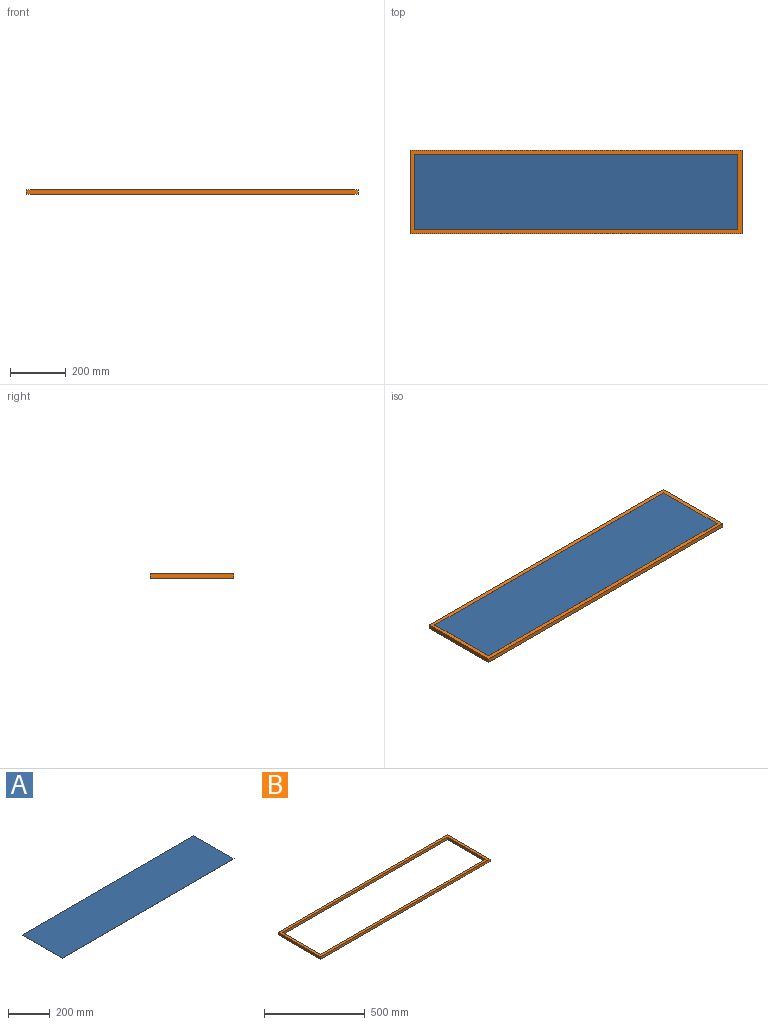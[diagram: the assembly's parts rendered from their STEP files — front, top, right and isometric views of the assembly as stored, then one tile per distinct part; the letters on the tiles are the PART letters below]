
ASSEMBLY  parts=2 mates=1
PART A: 6 faces, bbox 1160x270x1 mm
  f0: plane 270x1mm, normal (-1,0,0), area 270mm2, adj f1,f3,f4,f5
  f1: plane 1160x1mm, normal (0,-1,0), area 1160mm2, adj f0,f2,f4,f5
  f2: plane 270x1mm, normal (1,0,0), area 270mm2, adj f1,f3,f4,f5
  f3: plane 1160x1mm, normal (0,1,0), area 1160mm2, adj f0,f2,f4,f5
  f4: plane 1160x270mm, normal (0,0,1), area 313200mm2, adj f0,f1,f2,f3
  f5: plane 1160x270mm, normal (0,0,-1), area 313200mm2, adj f0,f1,f2,f3
PART B: 10 faces, bbox 1190x300x15 mm
  f0: plane 270x15mm, normal (1,0,0), area 4050mm2, adj f1,f7,f8,f9
  f1: plane 1160x15mm, normal (0,-1,0), area 17400mm2, adj f0,f2,f8,f9
  f2: plane 270x15mm, normal (-1,0,0), area 4050mm2, adj f1,f7,f8,f9
  f3: plane 300x15mm, normal (-1,0,0), area 4500mm2, adj f4,f6,f8,f9
  f4: plane 1190x15mm, normal (0,-1,0), area 17850mm2, adj f3,f5,f8,f9
  f5: plane 300x15mm, normal (1,0,0), area 4500mm2, adj f4,f6,f8,f9
  f6: plane 1190x15mm, normal (0,1,0), area 17850mm2, adj f3,f5,f8,f9
  f7: plane 1160x15mm, normal (0,1,0), area 17400mm2, adj f0,f2,f8,f9
  f8: plane 1190x300mm, normal (0,0,1), area 43800mm2, adj f0,f1,f2,f3,f4,f5,f6,f7
  f9: plane 1190x300mm, normal (0,0,-1), area 43800mm2, adj f0,f1,f2,f3,f4,f5,f6,f7
PLACE A t=(88.61,145.95,-158.12)mm
PLACE B t=(73.61,130.95,-172.12)mm
MATE fastened B.f8 <-> A.f4  axis (0,0,1) through (668.61,280.95,-157.12)mm
